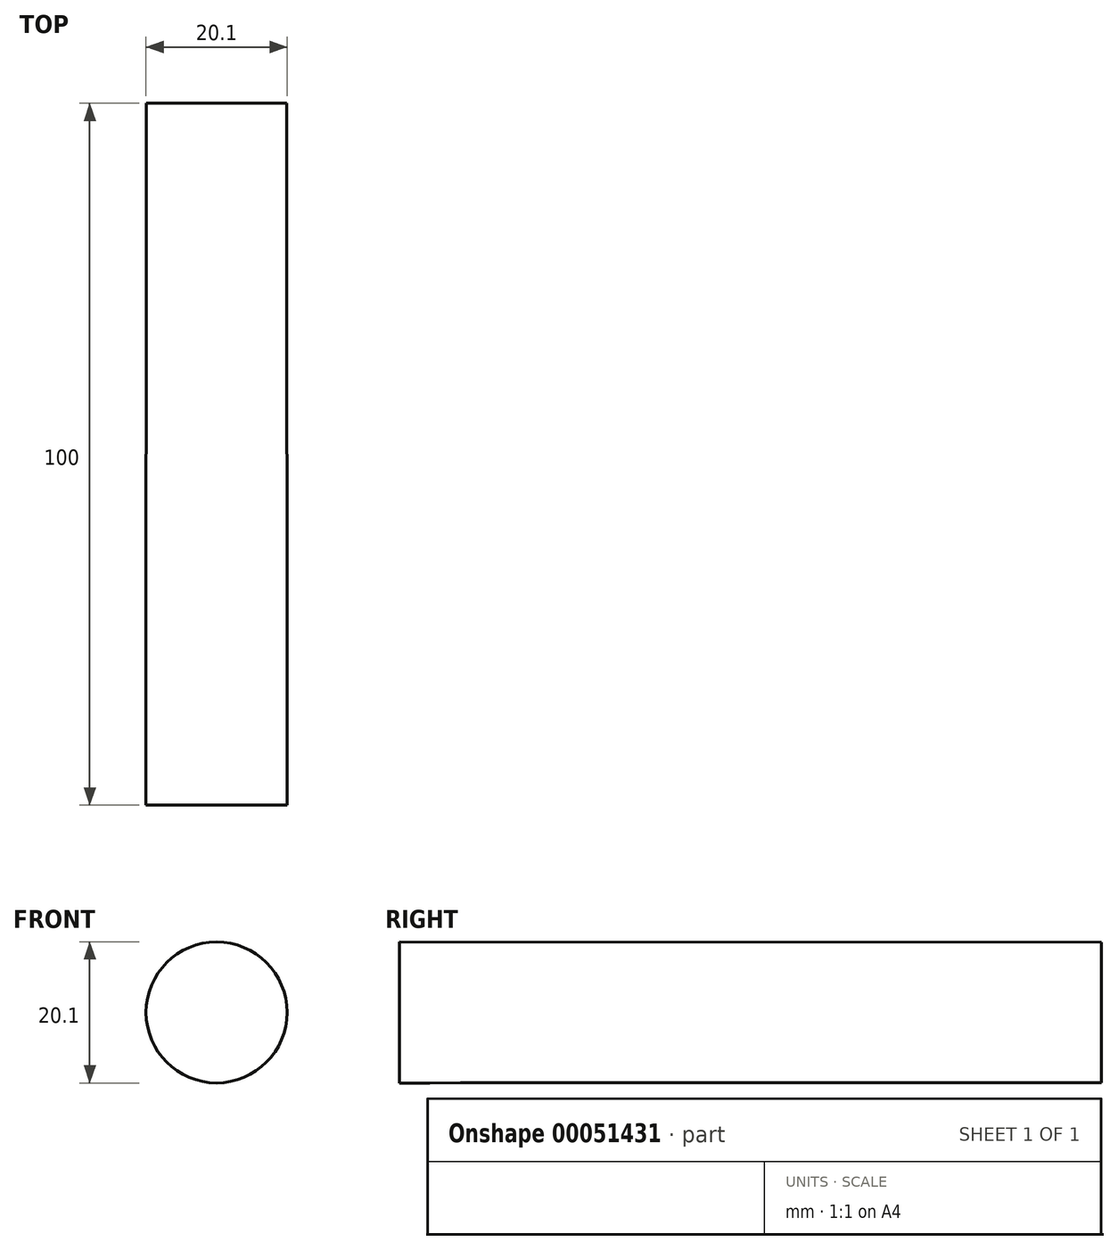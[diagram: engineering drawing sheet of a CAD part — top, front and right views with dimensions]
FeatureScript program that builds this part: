
annotation { "Feature Type Name" : "Feature", "Feature Type Description" : "" }
export const myFeature = defineFeature(function(context is Context, id is Id, definition is map)
    precondition{}
    {
        {
            var Q0;
            Q0=qCreatedBy(makeId("Front.planeOp"),FACE);
            var sketch = newSketch(context, id + "F0", { "sketchPlane" : qUnion([Q0])});
            skCircle(sketch, "E0", {"center": v(0, 0) * mm, "radius": 10 * mm});
            skSolve(sketch);
        }
        {
            var Q0;
            Q0=qCreatedBy(makeId("Front.planeOp"),FACE);
            cPlane(context, id + "F1", {"entities" : qUnion([Q0]), "cplaneType" : CPlaneType.OFFSET, "offset" : 100 * mm, "width" : 150 * mm, "height" : 150 * mm});
        }
        {
            var Q0;
            Q0=qCreatedBy(id+"F1.planeOp",FACE);
            var sketch = newSketch(context, id + "F2", { "sketchPlane" : qUnion([Q0])});
            skCircle(sketch, "E1", {"center": v(0, 0) * mm, "radius": 10.04 * mm});
            skSolve(sketch);
        }
        {
            var Q0;
            Q0=makeQuery(id+"F0.imprint","IMPRINT",FACE,{"disambiguationData":[TD([[makeQuery(id+"F0.imprint","IMPRINT",EDGE,{"derivedFrom":sQuery(id+"F0.wireOp",EDGE,"E0")}),1.0]])]});
            var Q1;
            Q1=makeQuery(id+"F2.imprint","IMPRINT",FACE,{"disambiguationData":[TD([[makeQuery(id+"F2.imprint","IMPRINT",EDGE,{"derivedFrom":sQuery(id+"F2.wireOp",EDGE,"E1")}),1.0]])]});
            loft(context, id + "F3", {"sheetProfilesArray" : [{ "sheetProfileEntities" : qUnion([Q0]) }, { "sheetProfileEntities" : qUnion([Q1]) }]});
        }
    });
